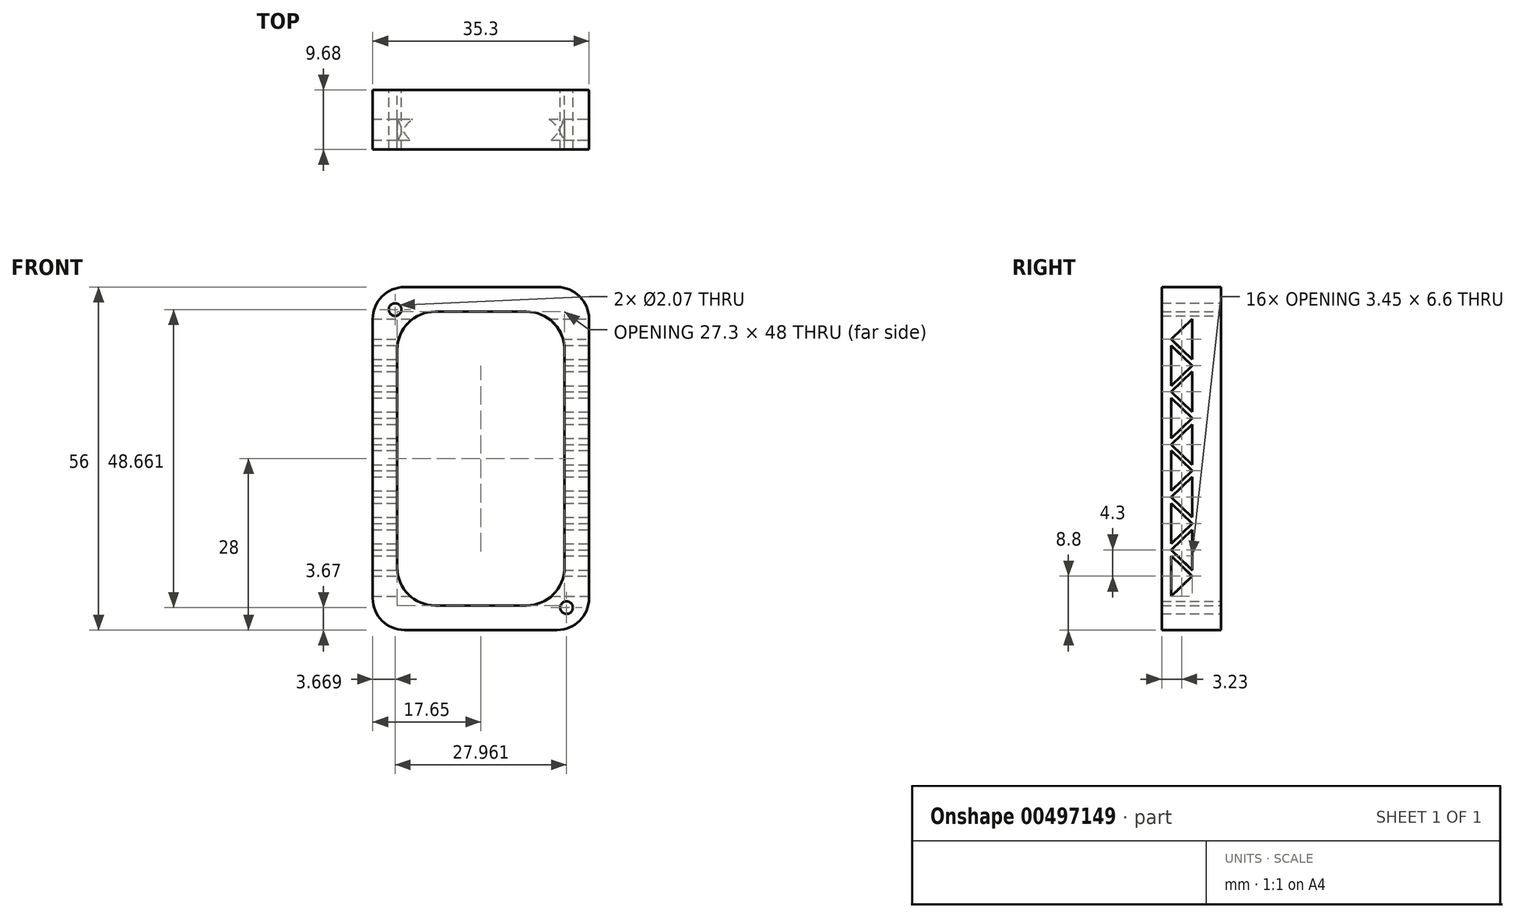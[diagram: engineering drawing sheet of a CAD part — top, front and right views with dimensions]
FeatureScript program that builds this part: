
annotation { "Feature Type Name" : "Feature", "Feature Type Description" : "" }
export const myFeature = defineFeature(function(context is Context, id is Id, definition is map)
    precondition{}
    {
        {
            var Q0;
            Q0=qCreatedBy(makeId("Front.planeOp"),FACE);
            var sketch = newSketch(context, id + "F0", { "sketchPlane" : qUnion([Q0])});
            skArc(sketch, "E0", {"start": v(17.65, 21.94) * mm, "mid": v(16.13, 25.62) * mm, "end": v(12.45, 27.14) * mm});
            skArc(sketch, "E1.MirrorCS", {"start": v(17.65, -23.66) * mm, "mid": v(16.13, -27.34) * mm, "end": v(12.45, -28.86) * mm});
            skArc(sketch, "E2.MirrorCS", {"start": v(-17.65, 21.94) * mm, "mid": v(-16.13, 25.62) * mm, "end": v(-12.45, 27.14) * mm});
            skArc(sketch, "E3.MirrorCS", {"start": v(-17.65, -23.66) * mm, "mid": v(-16.13, -27.34) * mm, "end": v(-12.45, -28.86) * mm});
            skLineSegment(sketch, "E4", {"start": v(-17.65, 21.94) * mm, "end": v(-17.65, -23.66) * mm});
            skLineSegment(sketch, "E5", {"start": v(-12.45, 27.14) * mm, "end": v(12.45, 27.14) * mm});
            skLineSegment(sketch, "E6", {"start": v(17.65, 21.94) * mm, "end": v(17.65, -23.66) * mm});
            skLineSegment(sketch, "E7", {"start": v(12.45, -28.86) * mm, "end": v(-12.45, -28.86) * mm});
            skLineSegment(sketch, "E8", {"start": v(-13.65, -18.66) * mm, "end": v(-13.65, 16.94) * mm});
            skLineSegment(sketch, "E9", {"start": v(-7.45, 23.14) * mm, "end": v(7.45, 23.14) * mm});
            skLineSegment(sketch, "E10", {"start": v(13.65, 16.94) * mm, "end": v(13.65, -18.66) * mm});
            skLineSegment(sketch, "E11", {"start": v(7.45, -24.86) * mm, "end": v(-7.45, -24.86) * mm});
            skArc(sketch, "E12.0", {"start": v(-13.65, -18.66) * mm, "mid": v(-11.83, -23.04) * mm, "end": v(-7.45, -24.86) * mm});
            skArc(sketch, "E13.0", {"start": v(13.65, -18.66) * mm, "mid": v(11.83, -23.04) * mm, "end": v(7.45, -24.86) * mm});
            skArc(sketch, "E14.0", {"start": v(13.65, 16.94) * mm, "mid": v(11.83, 21.32) * mm, "end": v(7.45, 23.14) * mm});
            skArc(sketch, "E15.0", {"start": v(-13.65, 16.94) * mm, "mid": v(-11.83, 21.32) * mm, "end": v(-7.45, 23.14) * mm});
            skCircle(sketch, "E16", {"center": v(-13.98, -25.2) * mm, "radius": 1.04 * mm});
            skCircle(sketch, "E17.MirrorC", {"center": v(13.98, -25.2) * mm, "radius": 1.04 * mm});
            skCircle(sketch, "E18.MirrorC", {"center": v(-13.98, 23.47) * mm, "radius": 1.04 * mm});
            skCircle(sketch, "E19.MirrorC", {"center": v(13.98, 23.47) * mm, "radius": 1.04 * mm});
            skSolve(sketch);
        }
        {
            var Q0;
            Q0 = qSketchRegion(id + "F0", true);
            extrude(context, id + "F1", {"entities" : qUnion([Q0]), "endBound" : BoundingType.SYMMETRIC, "depth" : 6.45 * mm, "offsetDistance" : 25 * mm});
        }
        {
            var Q0;
            Q0=makeQuery(id+"F0.imprint","IMPRINT",FACE,{"disambiguationData":[TD([[makeQuery(id+"F0.imprint","IMPRINT",EDGE,{"derivedFrom":sQuery(id+"F0.wireOp",EDGE,"E18.MirrorC")}),-1.0]])]});
            var Q1;
            Q1=makeQuery(id+"F0.imprint","IMPRINT",FACE,{"disambiguationData":[TD([[makeQuery(id+"F0.imprint","IMPRINT",EDGE,{"derivedFrom":sQuery(id+"F0.wireOp",EDGE,"E16")}),1.0]])]});
            var Q2;
            Q2=makeQuery(id+"F0.imprint","IMPRINT",FACE,{"disambiguationData":[TD([[makeQuery(id+"F0.imprint","IMPRINT",EDGE,{"derivedFrom":sQuery(id+"F0.wireOp",EDGE,"E19.MirrorC")}),1.0]])]});
            var Q3;
            Q3=makeQuery(id+"F0.imprint","IMPRINT",FACE,{"disambiguationData":[TD([[makeQuery(id+"F0.imprint","IMPRINT",EDGE,{"derivedFrom":sQuery(id+"F0.wireOp",EDGE,"E17.MirrorC")}),-1.0]])]});
            var Q4;
            Q4=makeQuery(id+"F1.opExtrude","CAP_FACE",FACE,{"disambiguationData":[OSD([sQuery(id+"F0.wireOp",EDGE,"E0"),sQuery(id+"F0.wireOp",EDGE,"E1.MirrorCS"),sQuery(id+"F0.wireOp",EDGE,"E2.MirrorCS"),sQuery(id+"F0.wireOp",EDGE,"E3.MirrorCS"),sQuery(id+"F0.wireOp",EDGE,"E4"),sQuery(id+"F0.wireOp",EDGE,"E5"),sQuery(id+"F0.wireOp",EDGE,"E6"),sQuery(id+"F0.wireOp",EDGE,"E7"),sQuery(id+"F0.wireOp",EDGE,"E8"),sQuery(id+"F0.wireOp",EDGE,"E9"),sQuery(id+"F0.wireOp",EDGE,"E10"),sQuery(id+"F0.wireOp",EDGE,"E11"),sQuery(id+"F0.wireOp",EDGE,"E12.0"),sQuery(id+"F0.wireOp",EDGE,"E13.0"),sQuery(id+"F0.wireOp",EDGE,"E14.0"),sQuery(id+"F0.wireOp",EDGE,"E15.0"),sQuery(id+"F0.wireOp",EDGE,"E16"),sQuery(id+"F0.wireOp",EDGE,"E17.MirrorC"),sQuery(id+"F0.wireOp",EDGE,"E18.MirrorC"),sQuery(id+"F0.wireOp",EDGE,"E19.MirrorC")])],"isStart":false});
            extrude(context, id + "F2", {"entities" : qUnion([Q0, Q1, Q2, Q3]), "operationType" : NewBodyOperationType.ADD, "oppositeDirection" : true, "depth" : 6.45 * mm, "offsetDistance" : 25 * mm, "hasSecondDirection" : true, "secondDirectionBound" : SecondDirectionBoundingType.UP_TO_SURFACE, "secondDirectionOppositeDirection" : false, "secondDirectionDepth" : 25 * mm, "secondDirectionBoundEntityFace" : qUnion([Q4])});
        }
        {
            var Q0;
            Q0=makeQuery(id+"F1.opExtrude","SWEPT_FACE",FACE,{"disambiguationData":[OSD([sQuery(id+"F0.wireOp",EDGE,"E6")])]});
            var sketch = newSketch(context, id + "F3", { "sketchPlane" : qUnion([Q0])});
            skLineSegment(sketch, "E20", {"start": v(-3.23, -23.66) * mm, "end": v(-3.23, -23.66) * mm});
            skLineSegment(sketch, "E21", {"start": v(-1.73, 18.64) * mm, "end": v(1.72, 21.94) * mm});
            skLineSegment(sketch, "E22", {"start": v(-1.72, 18.64) * mm, "end": v(1.72, 15.34) * mm});
            skLineSegment(sketch, "E23", {"start": v(1.72, 15.34) * mm, "end": v(1.72, 21.94) * mm});
            skLineSegment(sketch, "E24", {"start": v(1.72, 14.34) * mm, "end": v(-1.73, 17.64) * mm});
            skLineSegment(sketch, "E25.MirrorCS", {"start": v(1.72, 14.34) * mm, "end": v(-1.73, 11.04) * mm});
            skLineSegment(sketch, "E26", {"start": v(-1.73, 17.64) * mm, "end": v(-1.73, 11.04) * mm});
            skLineSegment(sketch, "E27.MirrorCS", {"start": v(1.72, 13.34) * mm, "end": v(1.72, 6.74) * mm});
            skLineSegment(sketch, "E28.MirrorCS", {"start": v(-1.73, 10.04) * mm, "end": v(1.72, 6.74) * mm});
            skLineSegment(sketch, "E29.MirrorCS", {"start": v(-1.72, 10.04) * mm, "end": v(1.72, 13.34) * mm});
            skLineSegment(sketch, "E30.MirrorCS", {"start": v(-1.73, 2.44) * mm, "end": v(-1.73, 9.04) * mm});
            skLineSegment(sketch, "E31.MirrorCS", {"start": v(1.72, 5.74) * mm, "end": v(-1.73, 9.04) * mm});
            skLineSegment(sketch, "E32.MirrorCS", {"start": v(1.72, 5.74) * mm, "end": v(-1.73, 2.44) * mm});
            skLineSegment(sketch, "E33.MirrorCS", {"start": v(-1.73, 1.44) * mm, "end": v(1.72, 4.74) * mm});
            skLineSegment(sketch, "E34.MirrorCS", {"start": v(-1.72, 1.44) * mm, "end": v(1.72, -1.86) * mm});
            skLineSegment(sketch, "E35.MirrorCS", {"start": v(1.72, -1.86) * mm, "end": v(1.72, 4.74) * mm});
            skLineSegment(sketch, "E36.MirrorCS", {"start": v(1.72, -2.86) * mm, "end": v(-1.73, 0.44) * mm});
            skLineSegment(sketch, "E37.MirrorCS", {"start": v(-1.73, 0.44) * mm, "end": v(-1.73, -6.16) * mm});
            skLineSegment(sketch, "E38.MirrorCS", {"start": v(1.73, -2.86) * mm, "end": v(-1.73, -6.16) * mm});
            skLineSegment(sketch, "E39.MirrorCS", {"start": v(-1.72, -7.16) * mm, "end": v(1.72, -3.86) * mm});
            skLineSegment(sketch, "E40.MirrorCS", {"start": v(-1.73, -7.16) * mm, "end": v(1.72, -10.46) * mm});
            skLineSegment(sketch, "E41.MirrorCS", {"start": v(1.72, -3.86) * mm, "end": v(1.72, -10.46) * mm});
            skLineSegment(sketch, "E42.MirrorCS", {"start": v(1.72, -11.46) * mm, "end": v(-1.73, -8.16) * mm});
            skLineSegment(sketch, "E43.MirrorCS", {"start": v(-1.73, -14.76) * mm, "end": v(-1.73, -8.16) * mm});
            skLineSegment(sketch, "E44.MirrorCS", {"start": v(1.72, -11.46) * mm, "end": v(-1.73, -14.76) * mm});
            skLineSegment(sketch, "E45.MirrorCS", {"start": v(-1.72, -15.76) * mm, "end": v(1.72, -12.46) * mm});
            skLineSegment(sketch, "E46.MirrorCS", {"start": v(-1.73, -15.76) * mm, "end": v(1.72, -19.06) * mm});
            skLineSegment(sketch, "E47.MirrorCS", {"start": v(1.72, -12.46) * mm, "end": v(1.72, -19.06) * mm});
            skLineSegment(sketch, "E48.MirrorCS", {"start": v(-1.73, -16.76) * mm, "end": v(-1.73, -23.36) * mm});
            skLineSegment(sketch, "E49.MirrorCS", {"start": v(-1.72, -15.76) * mm, "end": v(1.72, -19.06) * mm});
            skLineSegment(sketch, "E50.MirrorCS", {"start": v(1.73, -20.06) * mm, "end": v(-1.73, -16.76) * mm});
            skLineSegment(sketch, "E51.MirrorCS", {"start": v(1.73, -20.06) * mm, "end": v(-1.73, -23.36) * mm});
            skSolve(sketch);
        }
        {
            var Q0;
            Q0 = qSketchRegion(id + "F3", true);
            extrude(context, id + "F4", {"entities" : qUnion([Q0]), "operationType" : NewBodyOperationType.REMOVE, "endBound" : BoundingType.THROUGH_ALL, "oppositeDirection" : true, "depth" : 25 * mm, "offsetDistance" : 25 * mm});
        }
    });
